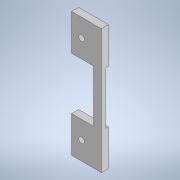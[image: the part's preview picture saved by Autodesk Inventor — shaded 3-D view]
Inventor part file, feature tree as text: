
AUTODESK INVENTOR PART (.ipt)
format: ipt  version: 2021 (Build 250183000, 183)  size: 137,728 bytes
history: native  units: in
note: dims shown in document units (in); Inventor stores cm internally (conversion verified against a paired STEP export)
features: reference x3, other x3, extrude x2, sketch x2, projected_geometry x1
ambient origin geometry x8: Origin, YZ Plane, XZ Plane, XY Plane, X Axis, Y Axis, Z Axis, Center Point
bodies: Solid1 (feature_tree)
feature tree (11):
  extrude  "Extrusion1"  Depth=0.0591in TaperAngle=0.0deg
  extrude  "Extrusion3"  [1 undecoded]
  sketch  "Sketch1"  dims[d1=0.0787in d2=0.0in d7=0.0591in d8=0.0in]
  reference  "Reference3"
  reference  "Reference4"
  reference  "Reference10"
  sketch  "Sketch3"
  projected_geometry  "Projected Loop3"
  parser-record x1  (decoder bookkeeping rows leaked as tree rows — omitted from the tree; the rows remain in map.json)
  other  "assembly.iam"
  other  "imu_plate:1"
note: 1 required parameter value undecoded (feature->parameter linkage not recoverable at this tier; creation-order binding heuristic only, values carry confidence <= 0.55)
note: 1 file-system path scrubbed to <path> (originals preserved in map.json)
